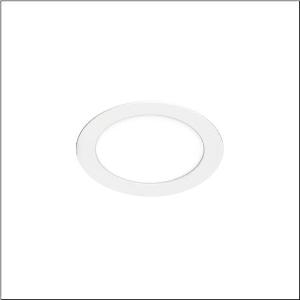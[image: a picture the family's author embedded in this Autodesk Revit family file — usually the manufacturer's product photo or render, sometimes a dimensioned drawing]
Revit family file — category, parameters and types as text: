
# Revit family: lunis_41_flat_51dr10dfgcb
name_source: partatom
category: Lighting Fixtures
units: mm (PartAtom-declared; Revit-internal decimal feet)

## family parameters
Cut with Voids When Loaded = No
Host = Face
Light Source = No
Part Type = Normal
Room Calculation Point = No
Round Connector Dimension = Use Diameter
Shared = No

## types (1)
- --- (1 x LED, 1550 lm, 11.5 W, 4000K)
    Apparent Load = 12 VA
    CIE Flux Codes = 49 80 96 100 100
    Color Rendering = 80
    Color Temperature = 4000K
    Default Elevation = 1800 mm
    Description = Lunis 41 Flat, downlight, light emission: direct distribution, LED rated luminous flux: 3.100lm, light colour: 830/840, control gear: ECG, mains connection: 230V, AC, 50/60Hz, housing, round, of aluminium, coated, traffic white (RAL 9016), diameter: 225mm, protection rating (complete): IP20, protection rating (on room side): IP44, insulation class (complete): insulation class II (safety insulation), certification: CE, permissible ambient temperature for indoor applications: -20..+40°C, packaging unit: 1 piece
    Height = 0 mm  [stored 0 ft]
    Lamp = 1 x LED
    Lamp Light Flux = 1550 lm
    Lamp Power = 11.5 W
    Lamp count = 1
    Length = 225 mm
    Luminous efficacy = 135 lm/W
    Manufacturer = Siteco
    ModVariant = No
    Model = 51DR10DFGCB
    Mounting Place = Ceiling
    Mounting Type = Recessed
    Number of Poles = 1
    OnlyDefault = Yes
    Power Factor = 1
    Product Name = Lunis 41 Flat
    Product group = downlight
    ProductGroupID = 401
    Protection Class = Protection class II
    Protection Degree = IP 20
    RLX_Detail_Level = 1
    RLX_Emergency_Light_Flux = 0 lm
    RLX_Emergency_Type = 0
    RLX_Emergency_Type_DB = No
    RlxData = <blob elided: 13817 chars, md5=d6af0276>
    Socket = socket
    Standby Power = 0 W
    System Light Flux = 1550 lm
    System Power = 12 W
    Type Comments = factory setting: colour temperature 4000K, luminous flux: 50 % | (ON | ON | ON) | 350 mA
    Type Image = l_1340923.jpg
    URL = http://relux.com
    VarID = @adj_021543
    Voltage = 0 V
    Weight = 0.00 kg
    Width = 0 mm  [stored 0 ft]

note: [stored X ft] marks values corroborated as IEEE doubles in the binary element streams (Revit-internal decimal feet)

## geometry (parser evidence)
native form markers: Sweep x11
no freeform markers — native parametric forms only
